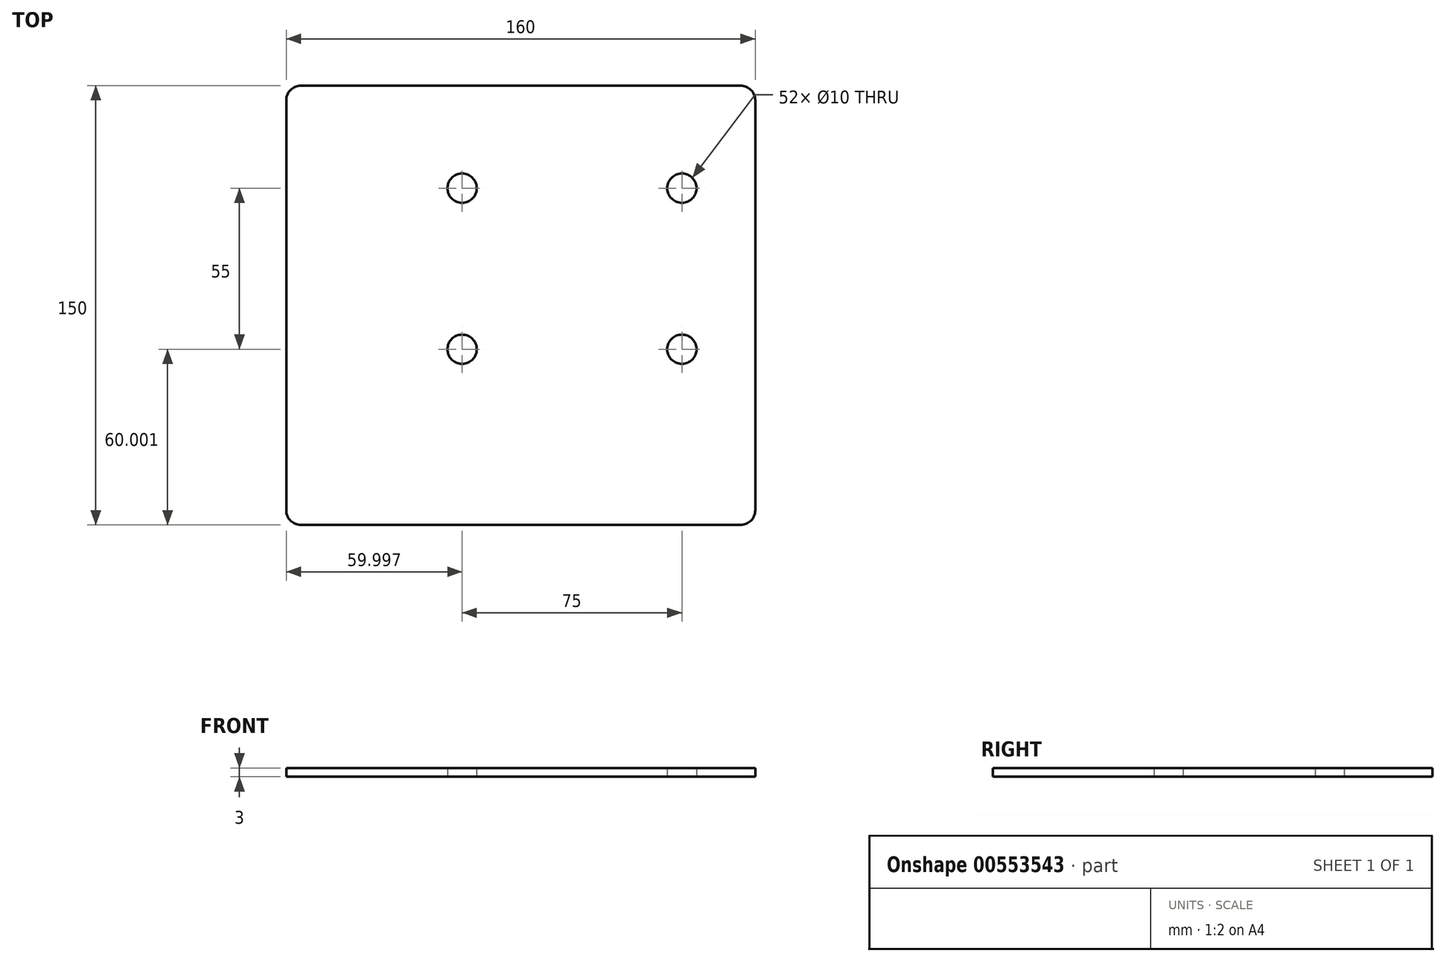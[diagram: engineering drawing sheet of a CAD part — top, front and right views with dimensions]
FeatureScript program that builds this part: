
annotation { "Feature Type Name" : "Feature", "Feature Type Description" : "" }
export const myFeature = defineFeature(function(context is Context, id is Id, definition is map)
    precondition{}
    {
        {
            var Q0;
            Q0=qCreatedBy(makeId("Top.planeOp"),FACE);
            var sketch = newSketch(context, id + "F0", { "sketchPlane" : qUnion([Q0])});
            skLineSegment(sketch, "E0.bottom", {"start": v(-175.16, 3.3) * mm, "end": v(-25.16, 3.3) * mm});
            skLineSegment(sketch, "E0.top", {"start": v(-175.16, -146.7) * mm, "end": v(-25.16, -146.7) * mm});
            skLineSegment(sketch, "E0.left", {"start": v(-180.16, -1.7) * mm, "end": v(-180.16, -141.7) * mm});
            skLineSegment(sketch, "E0.right", {"start": v(-20.16, -1.7) * mm, "end": v(-20.16, -141.7) * mm});
            skCircle(sketch, "E1", {"center": v(-120.16, -86.7) * mm, "radius": 5 * mm});
            skCircle(sketch, "E2.0.1.0", {"center": v(-120.16, -31.7) * mm, "radius": 5 * mm});
            skCircle(sketch, "E2.1.0.0", {"center": v(-45.16, -86.7) * mm, "radius": 5 * mm});
            skCircle(sketch, "E2.1.1.0", {"center": v(-45.16, -31.7) * mm, "radius": 5 * mm});
            skLineSegment(sketch, "E2.direction1", {"start": v(-120.16, -86.7) * mm, "end": v(-45.16, -86.7) * mm, "construction": true});
            skLineSegment(sketch, "E2.direction2", {"start": v(-120.16, -86.7) * mm, "end": v(-120.16, -31.7) * mm, "construction": true});
            skPoint(sketch, "E3.visualSharp", {"position": v(-20.16, 3.3) * mm});
            skArc(sketch, "E3.filletArc", {"start": v(-20.16, -1.7) * mm, "mid": v(-21.63, 1.84) * mm, "end": v(-25.16, 3.3) * mm});
            skPoint(sketch, "E4.visualSharp", {"position": v(-20.16, -146.7) * mm});
            skArc(sketch, "E4.filletArc", {"start": v(-25.16, -146.7) * mm, "mid": v(-21.63, -145.23) * mm, "end": v(-20.16, -141.7) * mm});
            skPoint(sketch, "E5.visualSharp", {"position": v(-180.16, -146.7) * mm});
            skArc(sketch, "E5.filletArc", {"start": v(-180.16, -141.7) * mm, "mid": v(-178.7, -145.23) * mm, "end": v(-175.16, -146.7) * mm});
            skPoint(sketch, "E6.visualSharp", {"position": v(-180.16, 3.3) * mm});
            skArc(sketch, "E6.filletArc", {"start": v(-175.16, 3.3) * mm, "mid": v(-178.7, 1.84) * mm, "end": v(-180.16, -1.7) * mm});
            skSolve(sketch);
        }
        {
            var Q0;
            Q0=makeQuery(id+"F0.imprint","IMPRINT",FACE,{"disambiguationData":[TD([[makeQuery(id+"F0.imprint","IMPRINT",EDGE,{"derivedFrom":sQuery(id+"F0.wireOp",EDGE,"E0.bottom")}),-1.0]])]});
            extrude(context, id + "F1", {"entities" : qUnion([Q0]), "depth" : 3 * mm, "offsetDistance" : 25 * mm});
        }
    });
